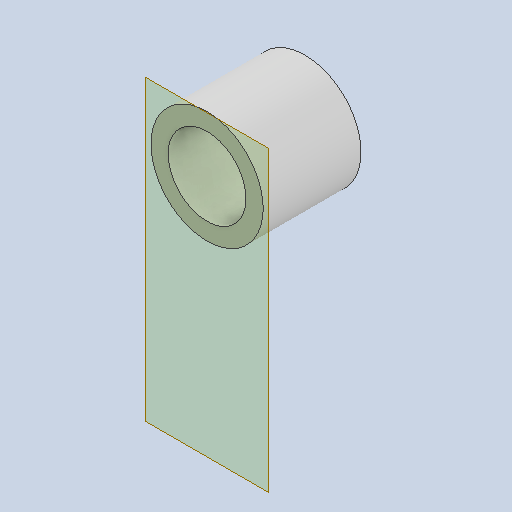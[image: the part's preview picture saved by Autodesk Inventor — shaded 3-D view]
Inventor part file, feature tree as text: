
AUTODESK INVENTOR PART (.ipt)
format: ipt  version: 2023 (Build 270158000, 158)  size: 241,152 bytes
history: native  units: mm
features: other x4, reference x2, plane x1, extrude x1, sketch x1
ambient origin geometry x8: Origin, YZ Plane, XZ Plane, XY Plane, X Axis, Y Axis, Z Axis, Center Point
bodies: Solid1 (feature_tree)
feature tree (9):
  plane  "Work Plane1"
  extrude  "Extrusion1"  [1 undecoded]
  sketch  "Sketch1"  dims[d0=16.0mm d1=0.0mm]
  reference  "Reference1"
  reference  "Reference2"
  parser-record x1  (decoder bookkeeping rows leaked as tree rows — omitted from the tree; the rows remain in map.json)
  other  "doorLockAssembly_V3.iam"
  other  "spacerA_V3:1"
  other  "tempMotorHolder_V3:1"
note: 1 required parameter value undecoded (feature->parameter linkage not recoverable at this tier; creation-order binding heuristic only, values carry confidence <= 0.55)
note: 1 file-system path scrubbed to <path> (originals preserved in map.json)
